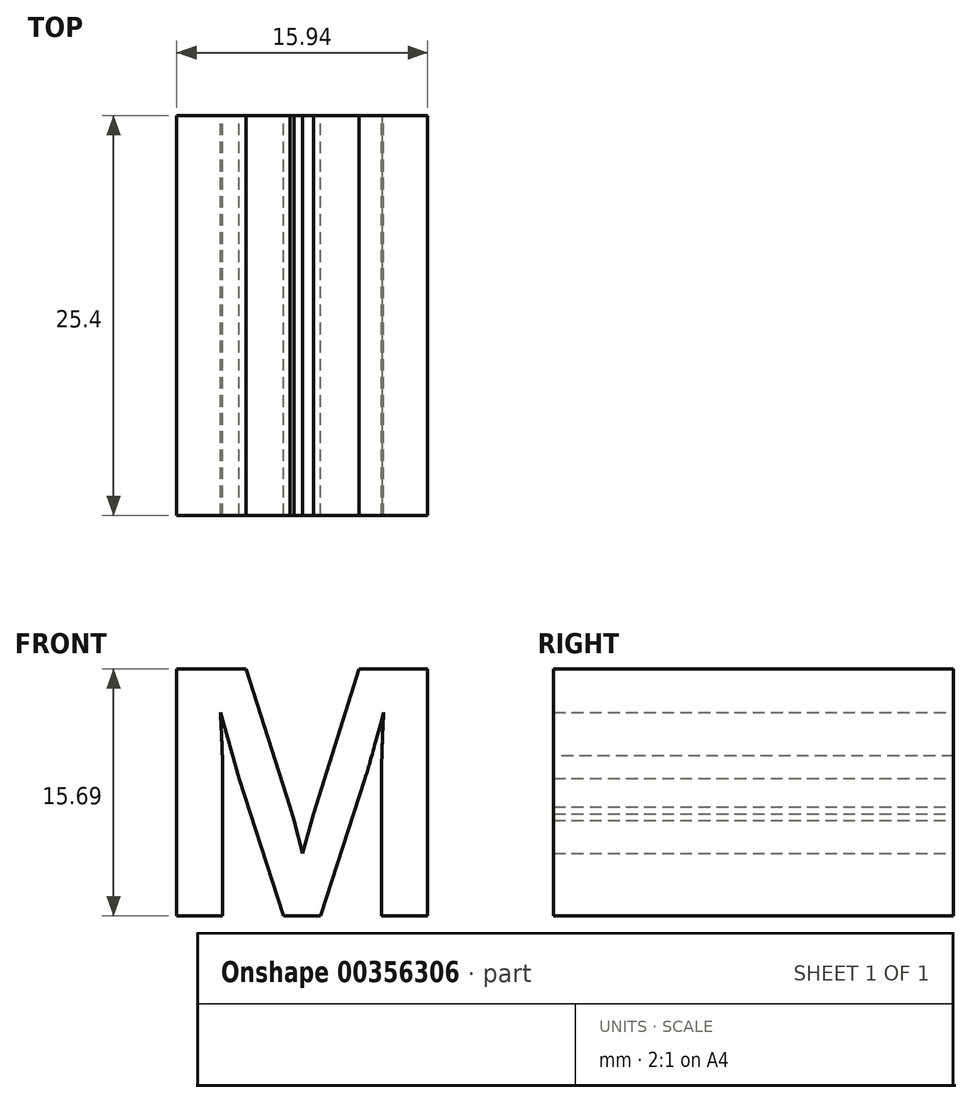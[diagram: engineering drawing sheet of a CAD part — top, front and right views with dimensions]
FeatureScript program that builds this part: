
annotation { "Feature Type Name" : "Feature", "Feature Type Description" : "" }
export const myFeature = defineFeature(function(context is Context, id is Id, definition is map)
    precondition{}
    {
        {
            var Q0;
            Q0=qCreatedBy(makeId("Front.planeOp"),FACE);
            var sketch = newSketch(context, id + "F0", { "sketchPlane" : qUnion([Q0])});
            skText(sketch, "E0", { "text": "M\n", "fontName": "Arimo-Bold.ttf"});
            const initialGuessF0  = {"E0": [-0.0109, -0.00883, 1, 0, 0.01642]};
            skSetInitialGuess(sketch, initialGuessF0);
            skSolve(sketch);
        }
        {
            var Q0;
            Q0=qSketchRegion(id+"F0",true);
            extrude(context, id + "F1", {"entities" : qUnion([Q0]), "depth" : 25.4 * mm});
        }
    });
